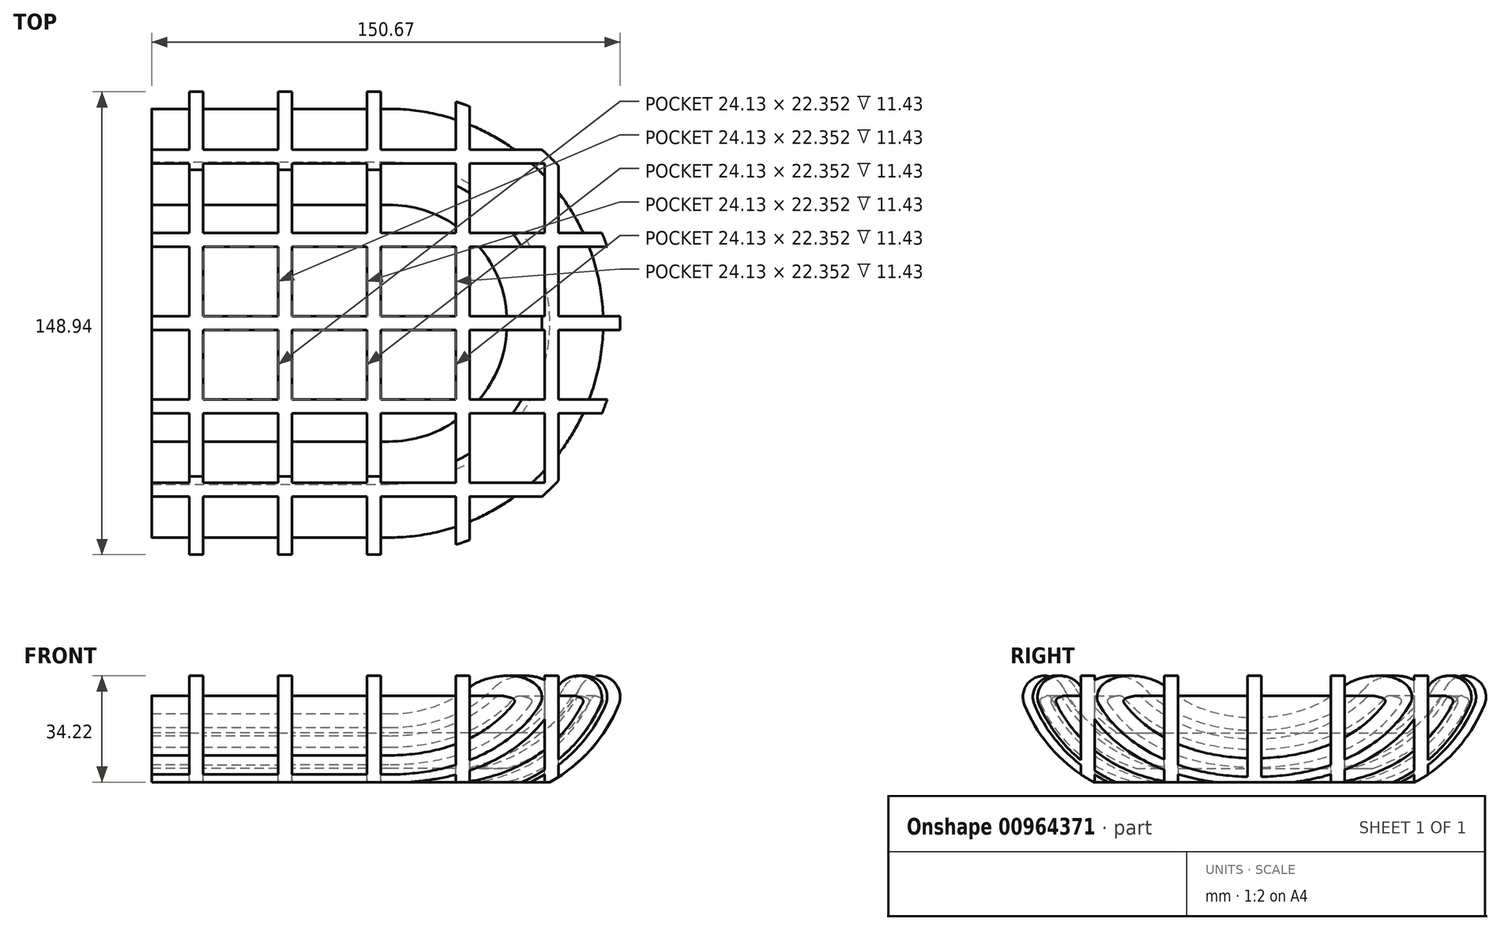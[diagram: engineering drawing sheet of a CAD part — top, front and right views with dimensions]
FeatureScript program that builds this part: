
annotation { "Feature Type Name" : "Feature", "Feature Type Description" : "" }
export const myFeature = defineFeature(function(context is Context, id is Id, definition is map)
    precondition{}
    {
        {
            var Q0;
            Q0=qCreatedBy(makeId("Top.planeOp"),FACE);
            var sketch = newSketch(context, id + "F0", { "sketchPlane" : qUnion([Q0])});
            skArc(sketch, "E0", {"start": v(-76.2, 38.1) * mm, "mid": v(-114.3, 0) * mm, "end": v(-76.2, -38.1) * mm});
            skArc(sketch, "E1", {"start": v(76.2, -38.1) * mm, "mid": v(114.3, 0) * mm, "end": v(76.2, 38.1) * mm});
            skLineSegment(sketch, "E2", {"start": v(-76.2, 38.1) * mm, "end": v(76.2, 38.1) * mm});
            skLineSegment(sketch, "E3", {"start": v(-76.2, -38.1) * mm, "end": v(76.2, -38.1) * mm});
            skLineSegment(sketch, "E4", {"start": v(-76.2, 0) * mm, "end": v(0, 0) * mm, "construction": true});
            skLineSegment(sketch, "E5", {"start": v(76.2, 0) * mm, "end": v(0, 0) * mm, "construction": true});
            skSolve(sketch);
        }
        {
            var Q0;
            Q0=qSketchRegion(id+"F0",true);
            extrude(context, id + "F1", {"entities" : qUnion([Q0]), "depth" : 4.44 * mm, "offsetDistance" : 25.4 * mm});
        }
        {
            var Q0;
            Q0=qCreatedBy(makeId("Right.planeOp"),FACE);
            var Q1;
            Q1=sQuery(id+"F0.wireOp",VERTEX,"E0.end");
            cPlane(context, id + "F2", {"entities" : qUnion([Q0, Q1]), "cplaneType" : CPlaneType.PLANE_POINT, "offset" : 25.4 * mm, "width" : 152.4 * mm, "height" : 152.4 * mm});
        }
        {
            var Q0;
            Q0=qCreatedBy(id+"F2.planeOp",FACE);
            var sketch = newSketch(context, id + "F3", { "sketchPlane" : qUnion([Q0])});
            skArc(sketch, "E6", {"start": v(-69.38, 26.7) * mm, "mid": v(-56.98, 9.56) * mm, "end": v(-38.1, 0) * mm});
            skArc(sketch, "E7", {"start": v(-65.92, 28.11) * mm, "mid": v(-54.33, 13.55) * mm, "end": v(-38.1, 4.44) * mm});
            skLineSegment(sketch, "E8", {"start": v(-65.92, 28.11) * mm, "end": v(-69.38, 26.7) * mm});
            skLineSegment(sketch, "E9", {"start": v(-38.1, 4.45) * mm, "end": v(-38.1, 0) * mm});
            skSolve(sketch);
        }
        {
            var Q0;
            Q0=makeQuery(id+"F3.imprint","IMPRINT",FACE,{"disambiguationData":[TD([[makeQuery(id+"F3.imprint","IMPRINT",EDGE,{"derivedFrom":sQuery(id+"F3.wireOp",EDGE,"E6")}),1.0]])]});
            var Q1;
            Q1=sQuery(id+"F0.wireOp",EDGE,"E0");
            var Q2;
            Q2=sQuery(id+"F0.wireOp",EDGE,"E2");
            var Q3;
            Q3=sQuery(id+"F0.wireOp",EDGE,"E1");
            var Q4;
            Q4=sQuery(id+"F0.wireOp",EDGE,"E3");
            sweep(context, id + "F4", {"profiles" : qUnion([Q0]), "path" : qUnion([Q1, Q2, Q3, Q4])});
        }
        {
            var Q0;
            Q0=qCreatedBy(makeId("Top.planeOp"),FACE);
            cPlane(context, id + "F5", {"entities" : qUnion([Q0]), "cplaneType" : CPlaneType.OFFSET, "offset" : 50.8 * mm, "width" : 152.4 * mm, "height" : 152.4 * mm});
        }
        {
            var Q0;
            Q0=qCreatedBy(id+"F5.planeOp",FACE);
            var sketch = newSketch(context, id + "F6", { "sketchPlane" : qUnion([Q0])});
            skLineSegment(sketch, "E10.bottom", {"start": v(-159.38, 120.18) * mm, "end": v(-154.94, 120.18) * mm});
            skLineSegment(sketch, "E10.top", {"start": v(-159.38, -120.18) * mm, "end": v(-154.94, -120.18) * mm});
            skLineSegment(sketch, "E10.left", {"start": v(-159.38, 120.18) * mm, "end": v(-159.38, -120.18) * mm});
            skLineSegment(sketch, "E10.right", {"start": v(-154.94, 120.18) * mm, "end": v(-154.94, -120.18) * mm});
            skLineSegment(sketch, "E11.bottom", {"start": v(-130.8, 120.18) * mm, "end": v(-126.37, 120.18) * mm});
            skLineSegment(sketch, "E11.top", {"start": v(-130.8, -120.18) * mm, "end": v(-126.36, -120.18) * mm});
            skLineSegment(sketch, "E11.left", {"start": v(-130.8, 120.18) * mm, "end": v(-130.8, -120.18) * mm});
            skLineSegment(sketch, "E11.right", {"start": v(-126.37, 120.18) * mm, "end": v(-126.37, -120.18) * mm});
            skLineSegment(sketch, "E12.bottom", {"start": v(-102.23, 120.18) * mm, "end": v(-97.79, 120.18) * mm});
            skLineSegment(sketch, "E12.top", {"start": v(-102.23, -120.18) * mm, "end": v(-97.79, -120.18) * mm});
            skLineSegment(sketch, "E12.left", {"start": v(-102.23, 120.18) * mm, "end": v(-102.23, -120.18) * mm});
            skLineSegment(sketch, "E12.right", {"start": v(-97.79, 120.18) * mm, "end": v(-97.79, -120.18) * mm});
            skLineSegment(sketch, "E13.bottom", {"start": v(-73.66, 120.18) * mm, "end": v(-69.21, 120.18) * mm});
            skLineSegment(sketch, "E13.top", {"start": v(-73.66, -120.18) * mm, "end": v(-69.21, -120.18) * mm});
            skLineSegment(sketch, "E13.left", {"start": v(-73.66, 120.18) * mm, "end": v(-73.66, -120.18) * mm});
            skLineSegment(sketch, "E13.right", {"start": v(-69.21, 120.18) * mm, "end": v(-69.21, -120.18) * mm});
            skLineSegment(sketch, "E14.bottom", {"start": v(-45.08, 120.18) * mm, "end": v(-40.64, 120.18) * mm});
            skLineSegment(sketch, "E14.top", {"start": v(-45.08, -120.18) * mm, "end": v(-40.64, -120.18) * mm});
            skLineSegment(sketch, "E14.left", {"start": v(-45.08, 120.18) * mm, "end": v(-45.08, -120.18) * mm});
            skLineSegment(sketch, "E14.right", {"start": v(-40.64, 120.18) * mm, "end": v(-40.64, -120.18) * mm});
            skLineSegment(sketch, "E15", {"start": v(-154.94, 120.18) * mm, "end": v(-130.8, 120.18) * mm, "construction": true});
            skLineSegment(sketch, "E16", {"start": v(-126.37, 120.18) * mm, "end": v(-102.23, 120.18) * mm, "construction": true});
            skLineSegment(sketch, "E17", {"start": v(-69.21, 120.18) * mm, "end": v(-45.08, 120.18) * mm, "construction": true});
            skLineSegment(sketch, "E18", {"start": v(-97.79, 120.18) * mm, "end": v(-73.66, 120.18) * mm, "construction": true});
            skLineSegment(sketch, "E19", {"start": v(0, 0) * mm, "end": v(-159.38, 0) * mm, "construction": true});
            skLineSegment(sketch, "E20", {"start": v(-40.64, 120.18) * mm, "end": v(-16.5, 120.18) * mm, "construction": true});
            skLineSegment(sketch, "E21.bottom", {"start": v(-16.5, 120.18) * mm, "end": v(-12.06, 120.18) * mm});
            skLineSegment(sketch, "E21.top", {"start": v(-16.5, -120.18) * mm, "end": v(-12.06, -120.18) * mm});
            skLineSegment(sketch, "E21.left", {"start": v(-16.5, 120.18) * mm, "end": v(-16.51, -120.18) * mm});
            skLineSegment(sketch, "E21.right", {"start": v(-12.06, 120.18) * mm, "end": v(-12.07, -120.18) * mm});
            skLineSegment(sketch, "E22.bottom", {"start": v(12.07, 120.18) * mm, "end": v(16.51, 120.18) * mm});
            skLineSegment(sketch, "E22.top", {"start": v(12.07, -120.18) * mm, "end": v(16.51, -120.18) * mm});
            skLineSegment(sketch, "E22.left", {"start": v(12.07, 120.18) * mm, "end": v(12.07, -120.18) * mm});
            skLineSegment(sketch, "E22.right", {"start": v(16.51, 120.18) * mm, "end": v(16.51, -120.18) * mm});
            skLineSegment(sketch, "E23.bottom", {"start": v(40.64, 120.18) * mm, "end": v(45.09, 120.18) * mm});
            skLineSegment(sketch, "E23.top", {"start": v(40.64, -120.18) * mm, "end": v(45.09, -120.18) * mm});
            skLineSegment(sketch, "E23.left", {"start": v(40.64, 120.18) * mm, "end": v(40.64, -120.18) * mm});
            skLineSegment(sketch, "E23.right", {"start": v(45.09, 120.18) * mm, "end": v(45.09, -120.18) * mm});
            skLineSegment(sketch, "E24.bottom", {"start": v(69.22, 120.18) * mm, "end": v(73.66, 120.18) * mm});
            skLineSegment(sketch, "E24.top", {"start": v(69.22, -120.18) * mm, "end": v(73.66, -120.18) * mm});
            skLineSegment(sketch, "E24.left", {"start": v(69.22, 120.18) * mm, "end": v(69.22, -120.18) * mm});
            skLineSegment(sketch, "E24.right", {"start": v(73.66, 120.18) * mm, "end": v(73.66, -120.18) * mm});
            skLineSegment(sketch, "E25.bottom", {"start": v(97.8, 120.18) * mm, "end": v(102.24, 120.18) * mm});
            skLineSegment(sketch, "E25.top", {"start": v(97.8, -120.18) * mm, "end": v(102.24, -120.18) * mm});
            skLineSegment(sketch, "E25.left", {"start": v(97.8, 120.18) * mm, "end": v(97.8, -120.18) * mm});
            skLineSegment(sketch, "E25.right", {"start": v(102.24, 120.18) * mm, "end": v(102.24, -120.18) * mm});
            skLineSegment(sketch, "E26.bottom", {"start": v(126.37, 120.18) * mm, "end": v(130.81, 120.18) * mm});
            skLineSegment(sketch, "E26.top", {"start": v(126.37, -120.18) * mm, "end": v(130.81, -120.18) * mm});
            skLineSegment(sketch, "E26.left", {"start": v(126.37, 120.18) * mm, "end": v(126.37, -120.18) * mm});
            skLineSegment(sketch, "E26.right", {"start": v(130.81, 120.18) * mm, "end": v(130.81, -120.18) * mm});
            skLineSegment(sketch, "E27", {"start": v(102.24, 120.18) * mm, "end": v(126.37, 120.18) * mm, "construction": true});
            skLineSegment(sketch, "E28", {"start": v(73.66, 120.18) * mm, "end": v(97.8, 120.18) * mm, "construction": true});
            skLineSegment(sketch, "E29", {"start": v(45.09, 120.18) * mm, "end": v(69.22, 120.18) * mm, "construction": true});
            skLineSegment(sketch, "E30", {"start": v(16.51, 120.18) * mm, "end": v(40.64, 120.18) * mm, "construction": true});
            skLineSegment(sketch, "E31", {"start": v(-12.06, 120.18) * mm, "end": v(12.07, 120.18) * mm, "construction": true});
            skLineSegment(sketch, "E32", {"start": v(-12.06, 0) * mm, "end": v(0, 69.38) * mm, "construction": true});
            skLineSegment(sketch, "E33", {"start": v(0, 69.38) * mm, "end": v(12.07, 0) * mm, "construction": true});
            skLineSegment(sketch, "E34.bottom", {"start": v(154.94, 120.18) * mm, "end": v(159.39, 120.18) * mm});
            skLineSegment(sketch, "E34.top", {"start": v(154.94, -120.18) * mm, "end": v(159.39, -120.18) * mm});
            skLineSegment(sketch, "E34.left", {"start": v(154.94, 120.18) * mm, "end": v(154.94, -120.18) * mm});
            skLineSegment(sketch, "E34.right", {"start": v(159.39, 120.18) * mm, "end": v(159.39, -120.18) * mm});
            skLineSegment(sketch, "E35", {"start": v(130.81, 120.18) * mm, "end": v(154.94, 120.18) * mm});
            skSolve(sketch);
        }
        {
            var Q0;
            Q0=qSketchRegion(id+"F6",true);
            extrude(context, id + "F7", {"entities" : qUnion([Q0]), "oppositeDirection" : true, "depth" : 63.5 * mm, "offsetDistance" : 25.4 * mm});
        }
        {
            var Q0;
            Q0=qCreatedBy(id+"F5.planeOp",FACE);
            var sketch = newSketch(context, id + "F8", { "sketchPlane" : qUnion([Q0])});
            skLineSegment(sketch, "E36.bottom", {"start": v(-183.68, 2.22) * mm, "end": v(183.68, 2.22) * mm});
            skLineSegment(sketch, "E36.top", {"start": v(-183.68, -2.22) * mm, "end": v(183.68, -2.22) * mm});
            skLineSegment(sketch, "E36.left", {"start": v(-183.68, 2.22) * mm, "end": v(-183.68, -2.22) * mm});
            skLineSegment(sketch, "E36.right", {"start": v(183.68, 2.22) * mm, "end": v(183.68, -2.22) * mm});
            skLineSegment(sketch, "E37.bottom", {"start": v(-183.68, 29.02) * mm, "end": v(183.68, 29.02) * mm});
            skLineSegment(sketch, "E37.top", {"start": v(-183.68, 24.57) * mm, "end": v(183.68, 24.57) * mm});
            skLineSegment(sketch, "E37.left", {"start": v(-183.68, 29.02) * mm, "end": v(-183.68, 24.57) * mm});
            skLineSegment(sketch, "E37.right", {"start": v(183.68, 29.02) * mm, "end": v(183.68, 24.57) * mm});
            skLineSegment(sketch, "E38.bottom", {"start": v(-183.68, 55.82) * mm, "end": v(183.68, 55.82) * mm});
            skLineSegment(sketch, "E38.top", {"start": v(-183.68, 51.37) * mm, "end": v(183.68, 51.37) * mm});
            skLineSegment(sketch, "E38.left", {"start": v(-183.68, 55.82) * mm, "end": v(-183.68, 51.37) * mm});
            skLineSegment(sketch, "E38.right", {"start": v(183.68, 55.82) * mm, "end": v(183.68, 51.37) * mm});
            skLineSegment(sketch, "E39.bottom", {"start": v(-183.68, -24.57) * mm, "end": v(183.68, -24.57) * mm});
            skLineSegment(sketch, "E39.top", {"start": v(-183.68, -29.02) * mm, "end": v(183.68, -29.02) * mm});
            skLineSegment(sketch, "E39.left", {"start": v(-183.68, -24.57) * mm, "end": v(-183.68, -29.02) * mm});
            skLineSegment(sketch, "E39.right", {"start": v(183.68, -24.57) * mm, "end": v(183.68, -29.02) * mm});
            skLineSegment(sketch, "E40.bottom", {"start": v(-183.68, -51.37) * mm, "end": v(183.68, -51.37) * mm});
            skLineSegment(sketch, "E40.top", {"start": v(-183.68, -55.82) * mm, "end": v(183.68, -55.82) * mm});
            skLineSegment(sketch, "E40.left", {"start": v(-183.68, -51.37) * mm, "end": v(-183.68, -55.82) * mm});
            skLineSegment(sketch, "E40.right", {"start": v(183.68, -51.37) * mm, "end": v(183.68, -55.82) * mm});
            skLineSegment(sketch, "E41", {"start": v(183.68, 51.37) * mm, "end": v(183.68, 29.02) * mm, "construction": true});
            skLineSegment(sketch, "E42", {"start": v(183.68, 24.57) * mm, "end": v(183.68, 2.22) * mm, "construction": true});
            skLineSegment(sketch, "E43", {"start": v(183.68, -2.22) * mm, "end": v(183.68, -24.57) * mm, "construction": true});
            skLineSegment(sketch, "E44", {"start": v(183.68, -29.02) * mm, "end": v(183.68, -51.37) * mm, "construction": true});
            skLineSegment(sketch, "E45", {"start": v(0, 0) * mm, "end": v(0, 2.22) * mm, "construction": true});
            skLineSegment(sketch, "E46", {"start": v(0, 0) * mm, "end": v(183.68, 0) * mm, "construction": true});
            skLineSegment(sketch, "E47", {"start": v(0, 0) * mm, "end": v(0, -2.22) * mm, "construction": true});
            skSolve(sketch);
        }
        {
            var Q0;
            Q0=qSketchRegion(id+"F8",true);
            extrude(context, id + "F9", {"entities" : qUnion([Q0]), "oppositeDirection" : true, "depth" : 63.5 * mm, "offsetDistance" : 25.4 * mm});
        }
        {
            var Q0;
            Q0=makeQuery(id+"F4.opSweep","SWEPT_EDGE",EDGE,{"disambiguationData":[OSD([sQuery(id+"F0.wireOp",EDGE,"E0"),sQuery(id+"F3.wireOp",EDGE,"E6"),sQuery(id+"F3.wireOp",EDGE,"E8")])]});
            fillet(context, id + "F10", {"entities" : qUnion([Q0]), "radius" : 1.27 * mm, "tangentPropagation" : true, "allowEdgeOverflow" : false});
        }
        {
            var Q0;
            Q0=makeQuery(id+"F4.opSweep","SWEPT_EDGE",EDGE,{"disambiguationData":[OSD([sQuery(id+"F0.wireOp",EDGE,"E0"),sQuery(id+"F3.wireOp",EDGE,"E7"),sQuery(id+"F3.wireOp",EDGE,"E8")])]});
            fillet(context, id + "F11", {"entities" : qUnion([Q0]), "radius" : 1.27 * mm, "tangentPropagation" : true, "allowEdgeOverflow" : false});
        }
        {
            var Q0;
            Q0=makeQuery(id+"F4.opSweep","SWEPT_BODY",BODY,{"disambiguationData":[OSD([sQuery(id+"F0.wireOp",EDGE,"E2"),sQuery(id+"F3.wireOp",EDGE,"E6"),sQuery(id+"F3.wireOp",EDGE,"E7"),sQuery(id+"F3.wireOp",EDGE,"E8"),sQuery(id+"F3.wireOp",EDGE,"E9")])]});
            var Q1;
            Q1=makeQuery(id+"F7.opExtrude","SWEPT_BODY",BODY,{"disambiguationData":[OSD([sQuery(id+"F6.wireOp",EDGE,"E10.bottom"),sQuery(id+"F6.wireOp",EDGE,"E10.top"),sQuery(id+"F6.wireOp",EDGE,"E10.left"),sQuery(id+"F6.wireOp",EDGE,"E10.right")])]});
            var Q2;
            Q2=makeQuery(id+"F7.opExtrude","SWEPT_BODY",BODY,{"disambiguationData":[OSD([sQuery(id+"F6.wireOp",EDGE,"E11.bottom"),sQuery(id+"F6.wireOp",EDGE,"E11.top"),sQuery(id+"F6.wireOp",EDGE,"E11.left"),sQuery(id+"F6.wireOp",EDGE,"E11.right")])]});
            var Q3;
            Q3=makeQuery(id+"F7.opExtrude","SWEPT_BODY",BODY,{"disambiguationData":[OSD([sQuery(id+"F6.wireOp",EDGE,"E12.bottom"),sQuery(id+"F6.wireOp",EDGE,"E12.top"),sQuery(id+"F6.wireOp",EDGE,"E12.left"),sQuery(id+"F6.wireOp",EDGE,"E12.right")])]});
            var Q4;
            Q4=makeQuery(id+"F7.opExtrude","SWEPT_BODY",BODY,{"disambiguationData":[OSD([sQuery(id+"F6.wireOp",EDGE,"E13.bottom"),sQuery(id+"F6.wireOp",EDGE,"E13.top"),sQuery(id+"F6.wireOp",EDGE,"E13.left"),sQuery(id+"F6.wireOp",EDGE,"E13.right")])]});
            var Q5;
            Q5=makeQuery(id+"F7.opExtrude","SWEPT_BODY",BODY,{"disambiguationData":[OSD([sQuery(id+"F6.wireOp",EDGE,"E14.bottom"),sQuery(id+"F6.wireOp",EDGE,"E14.top"),sQuery(id+"F6.wireOp",EDGE,"E14.left"),sQuery(id+"F6.wireOp",EDGE,"E14.right")])]});
            var Q6;
            Q6=makeQuery(id+"F7.opExtrude","SWEPT_BODY",BODY,{"disambiguationData":[OSD([sQuery(id+"F6.wireOp",EDGE,"E21.bottom"),sQuery(id+"F6.wireOp",EDGE,"E21.top"),sQuery(id+"F6.wireOp",EDGE,"E21.left"),sQuery(id+"F6.wireOp",EDGE,"E21.right")])]});
            var Q7;
            Q7=makeQuery(id+"F7.opExtrude","SWEPT_BODY",BODY,{"disambiguationData":[OSD([sQuery(id+"F6.wireOp",EDGE,"E22.bottom"),sQuery(id+"F6.wireOp",EDGE,"E22.top"),sQuery(id+"F6.wireOp",EDGE,"E22.left"),sQuery(id+"F6.wireOp",EDGE,"E22.right")])]});
            var Q8;
            Q8=makeQuery(id+"F7.opExtrude","SWEPT_BODY",BODY,{"disambiguationData":[OSD([sQuery(id+"F6.wireOp",EDGE,"E23.bottom"),sQuery(id+"F6.wireOp",EDGE,"E23.top"),sQuery(id+"F6.wireOp",EDGE,"E23.left"),sQuery(id+"F6.wireOp",EDGE,"E23.right")])]});
            var Q9;
            Q9=makeQuery(id+"F7.opExtrude","SWEPT_BODY",BODY,{"disambiguationData":[OSD([sQuery(id+"F6.wireOp",EDGE,"E24.bottom"),sQuery(id+"F6.wireOp",EDGE,"E24.top"),sQuery(id+"F6.wireOp",EDGE,"E24.left"),sQuery(id+"F6.wireOp",EDGE,"E24.right")])]});
            var Q10;
            Q10=makeQuery(id+"F7.opExtrude","SWEPT_BODY",BODY,{"disambiguationData":[OSD([sQuery(id+"F6.wireOp",EDGE,"E25.bottom"),sQuery(id+"F6.wireOp",EDGE,"E25.top"),sQuery(id+"F6.wireOp",EDGE,"E25.left"),sQuery(id+"F6.wireOp",EDGE,"E25.right")])]});
            var Q11;
            Q11=makeQuery(id+"F7.opExtrude","SWEPT_BODY",BODY,{"disambiguationData":[OSD([sQuery(id+"F6.wireOp",EDGE,"E26.bottom"),sQuery(id+"F6.wireOp",EDGE,"E26.top"),sQuery(id+"F6.wireOp",EDGE,"E26.left"),sQuery(id+"F6.wireOp",EDGE,"E26.right")])]});
            var Q12;
            Q12=makeQuery(id+"F7.opExtrude","SWEPT_BODY",BODY,{"disambiguationData":[OSD([sQuery(id+"F6.wireOp",EDGE,"E34.bottom"),sQuery(id+"F6.wireOp",EDGE,"E34.top"),sQuery(id+"F6.wireOp",EDGE,"E34.left"),sQuery(id+"F6.wireOp",EDGE,"E34.right")])]});
            var Q13;
            Q13=makeQuery(id+"F9.opExtrude","SWEPT_BODY",BODY,{"disambiguationData":[OSD([sQuery(id+"F8.wireOp",EDGE,"E36.bottom"),sQuery(id+"F8.wireOp",EDGE,"E36.top"),sQuery(id+"F8.wireOp",EDGE,"E36.left"),sQuery(id+"F8.wireOp",EDGE,"E36.right")])]});
            var Q14;
            Q14=makeQuery(id+"F9.opExtrude","SWEPT_BODY",BODY,{"disambiguationData":[OSD([sQuery(id+"F8.wireOp",EDGE,"E37.bottom"),sQuery(id+"F8.wireOp",EDGE,"E37.top"),sQuery(id+"F8.wireOp",EDGE,"E37.left"),sQuery(id+"F8.wireOp",EDGE,"E37.right")])]});
            var Q15;
            Q15=makeQuery(id+"F9.opExtrude","SWEPT_BODY",BODY,{"disambiguationData":[OSD([sQuery(id+"F8.wireOp",EDGE,"E38.bottom"),sQuery(id+"F8.wireOp",EDGE,"E38.top"),sQuery(id+"F8.wireOp",EDGE,"E38.left"),sQuery(id+"F8.wireOp",EDGE,"E38.right")])]});
            var Q16;
            Q16=makeQuery(id+"F9.opExtrude","SWEPT_BODY",BODY,{"disambiguationData":[OSD([sQuery(id+"F8.wireOp",EDGE,"E39.bottom"),sQuery(id+"F8.wireOp",EDGE,"E39.top"),sQuery(id+"F8.wireOp",EDGE,"E39.left"),sQuery(id+"F8.wireOp",EDGE,"E39.right")])]});
            var Q17;
            Q17=makeQuery(id+"F9.opExtrude","SWEPT_BODY",BODY,{"disambiguationData":[OSD([sQuery(id+"F8.wireOp",EDGE,"E40.bottom"),sQuery(id+"F8.wireOp",EDGE,"E40.top"),sQuery(id+"F8.wireOp",EDGE,"E40.left"),sQuery(id+"F8.wireOp",EDGE,"E40.right")])]});
            var Q18;
            Q18=makeQuery(id+"F1.opExtrude","SWEPT_BODY",BODY,{"disambiguationData":[OSD([sQuery(id+"F0.wireOp",EDGE,"E0"),sQuery(id+"F0.wireOp",EDGE,"E1"),sQuery(id+"F0.wireOp",EDGE,"E2"),sQuery(id+"F0.wireOp",EDGE,"E3")])]});
            booleanBodies(context, id + "F12", {"operationType" : BooleanOperationType.UNION, "tools" : qUnion([Q0, Q1, Q2, Q3, Q4, Q5, Q6, Q7, Q8, Q9, Q10, Q11, Q12, Q13, Q14, Q15, Q16, Q17, Q18])});
        }
        {
            var Q0;
            Q0=qCreatedBy(id+"F2.planeOp",FACE);
            var sketch = newSketch(context, id + "F13", { "sketchPlane" : qUnion([Q0])});
            skArc(sketch, "E48", {"start": v(-61.6, 30.53) * mm, "mid": v(-70.5, 33.6) * mm, "end": v(-73.96, 24.82) * mm});
            skArc(sketch, "E49", {"start": v(-73.96, 24.82) * mm, "mid": v(-64.07, 9.48) * mm, "end": v(-49.31, -1.27) * mm});
            skLineSegment(sketch, "E50", {"start": v(-49.31, -1.27) * mm, "end": v(0, -1.27) * mm});
            skLineSegment(sketch, "E51", {"start": v(0, -1.27) * mm, "end": v(0, 0) * mm});
            skLineSegment(sketch, "E52", {"start": v(0, 0) * mm, "end": v(0, 15.88) * mm});
            skLineSegment(sketch, "E53", {"start": v(0, 15.88) * mm, "end": v(-49.31, 15.87) * mm});
            skArc(sketch, "E54", {"start": v(-61.6, 30.53) * mm, "mid": v(-56.27, 22.52) * mm, "end": v(-49.31, 15.88) * mm});
            skLineSegment(sketch, "E55", {"start": v(0, 15.88) * mm, "end": v(0, 76.2) * mm});
            skLineSegment(sketch, "E56", {"start": v(0, -1.27) * mm, "end": v(0, -38.1) * mm});
            skLineSegment(sketch, "E57", {"start": v(0, -38.1) * mm, "end": v(-158.28, -38.1) * mm});
            skLineSegment(sketch, "E58", {"start": v(-158.28, -38.1) * mm, "end": v(-158.28, 76.2) * mm});
            skLineSegment(sketch, "E59", {"start": v(-158.28, 76.2) * mm, "end": v(0, 76.2) * mm});
            skSolve(sketch);
        }
        {
            var Q0;
            Q0=qCreatedBy(id+"F2.planeOp",FACE);
            var sketch = newSketch(context, id + "F14", { "sketchPlane" : qUnion([Q0])});
            skArc(sketch, "E60.0", {"start": v(-61.6, 30.53) * mm, "mid": v(-56.27, 22.52) * mm, "end": v(-49.31, 15.88) * mm});
            skArc(sketch, "E60.1", {"start": v(-73.96, 24.82) * mm, "mid": v(-64.07, 9.48) * mm, "end": v(-49.31, -1.27) * mm});
            skArc(sketch, "E61.0", {"start": v(-61.6, 30.53) * mm, "mid": v(-70.5, 33.6) * mm, "end": v(-73.96, 24.82) * mm});
            skLineSegment(sketch, "E62", {"start": v(-49.31, 15.88) * mm, "end": v(-49.31, 76.2) * mm});
            skLineSegment(sketch, "E63", {"start": v(-49.31, 76.2) * mm, "end": v(-158.28, 76.2) * mm});
            skLineSegment(sketch, "E64", {"start": v(-158.28, 76.2) * mm, "end": v(-158.28, -38.1) * mm});
            skLineSegment(sketch, "E65", {"start": v(-158.28, -38.1) * mm, "end": v(-49.31, -38.1) * mm});
            skLineSegment(sketch, "E66", {"start": v(-49.31, -38.1) * mm, "end": v(-49.31, -1.27) * mm});
            skSolve(sketch);
        }
        {
            var Q0;
            Q0=makeQuery(id+"F14.imprint","IMPRINT",FACE,{"disambiguationData":[TD([[makeQuery(id+"F14.imprint","IMPRINT",EDGE,{"derivedFrom":sQuery(id+"F14.wireOp",EDGE,"E60.0")}),1.0]])]});
            var Q1;
            Q1=sQuery(id+"F0.wireOp",EDGE,"E0");
            var Q2;
            Q2=sQuery(id+"F0.wireOp",EDGE,"E2");
            var Q3;
            Q3=sQuery(id+"F0.wireOp",EDGE,"E1");
            var Q4;
            Q4=sQuery(id+"F0.wireOp",EDGE,"E3");
            sweep(context, id + "F15", {"operationType" : NewBodyOperationType.REMOVE, "profiles" : qUnion([Q0]), "path" : qUnion([Q1, Q2, Q3, Q4])});
        }
        {
            var Q0;
            Q0=qCreatedBy(makeId("Top.planeOp"),FACE);
            var Q1;
            Q1=sQuery(id+"F13.wireOp",VERTEX,"E53.end");
            cPlane(context, id + "F16", {"entities" : qUnion([Q0, Q1]), "cplaneType" : CPlaneType.PLANE_POINT, "offset" : 25.4 * mm, "width" : 152.4 * mm, "height" : 152.4 * mm});
        }
        {
            var Q0;
            Q0=qCreatedBy(makeId("Top.planeOp"),FACE);
            var Q1;
            Q1=sQuery(id+"F13.wireOp",VERTEX,"E49.end");
            cPlane(context, id + "F17", {"entities" : qUnion([Q0, Q1]), "cplaneType" : CPlaneType.PLANE_POINT, "offset" : 25.4 * mm, "width" : 152.4 * mm, "height" : 152.4 * mm});
        }
        {
            var Q0;
            Q0=qCreatedBy(id+"F16.planeOp",FACE);
            var sketch = newSketch(context, id + "F18", { "sketchPlane" : qUnion([Q0])});
            skArc(sketch, "E67", {"start": v(-76.2, 49.31) * mm, "mid": v(-125.51, 0) * mm, "end": v(-76.2, -49.31) * mm});
            skArc(sketch, "E68", {"start": v(76.2, -49.31) * mm, "mid": v(125.51, 0) * mm, "end": v(76.2, 49.31) * mm});
            skLineSegment(sketch, "E69", {"start": v(-76.2, 49.31) * mm, "end": v(76.2, 49.31) * mm});
            skLineSegment(sketch, "E70", {"start": v(-76.2, -49.31) * mm, "end": v(76.2, -49.31) * mm});
            skLineSegment(sketch, "E71", {"start": v(-76.2, 0) * mm, "end": v(0, 0) * mm, "construction": true});
            skLineSegment(sketch, "E72", {"start": v(0, 0) * mm, "end": v(76.2, 0) * mm, "construction": true});
            skSolve(sketch);
        }
        {
            var Q0;
            Q0=qCreatedBy(id+"F17.planeOp",FACE);
            var sketch = newSketch(context, id + "F19", { "sketchPlane" : qUnion([Q0])});
            skArc(sketch, "E73", {"start": v(-76.2, 49.31) * mm, "mid": v(-125.51, 0) * mm, "end": v(-76.2, -49.31) * mm});
            skArc(sketch, "E74", {"start": v(76.2, -49.31) * mm, "mid": v(125.51, 0) * mm, "end": v(76.2, 49.31) * mm});
            skLineSegment(sketch, "E75", {"start": v(-76.2, 49.31) * mm, "end": v(76.2, 49.31) * mm});
            skLineSegment(sketch, "E76", {"start": v(76.2, -49.31) * mm, "end": v(-76.2, -49.31) * mm});
            skLineSegment(sketch, "E77", {"start": v(-76.2, 0) * mm, "end": v(0, 0) * mm, "construction": true});
            skLineSegment(sketch, "E78", {"start": v(0, 0) * mm, "end": v(76.2, 0) * mm, "construction": true});
            skSolve(sketch);
        }
        {
            var Q0;
            Q0=qSketchRegion(id+"F18",true);
            extrude(context, id + "F20", {"entities" : qUnion([Q0]), "operationType" : NewBodyOperationType.REMOVE, "endBound" : BoundingType.THROUGH_ALL, "depth" : 25.4 * mm, "offsetDistance" : 25.4 * mm});
        }
        {
            var Q0;
            Q0=qSketchRegion(id+"F19",true);
            extrude(context, id + "F21", {"entities" : qUnion([Q0]), "operationType" : NewBodyOperationType.REMOVE, "endBound" : BoundingType.THROUGH_ALL, "oppositeDirection" : true, "depth" : 25.4 * mm, "offsetDistance" : 25.4 * mm});
        }
        {
            var Q0;
            Q0=makeQuery(id+"F12.opBoolean","SPLIT",FACE,{"disambiguationData":[TD([makeQuery(id+"F7.opExtrude","SWEPT_FACE",FACE,{"disambiguationData":[OSD([sQuery(id+"F6.wireOp",EDGE,"E21.right")])]}),makeQuery(id+"F7.opExtrude","SWEPT_FACE",FACE,{"disambiguationData":[OSD([sQuery(id+"F6.wireOp",EDGE,"E22.left")])]}),makeQuery(id+"F9.opExtrude","SWEPT_FACE",FACE,{"disambiguationData":[OSD([sQuery(id+"F8.wireOp",EDGE,"E36.top")])]}),makeQuery(id+"F9.opExtrude","SWEPT_FACE",FACE,{"disambiguationData":[OSD([sQuery(id+"F8.wireOp",EDGE,"E39.bottom")])]})])],"derivedFrom":makeQuery(id+"F1.opExtrude","CAP_FACE",FACE,{"disambiguationData":[OSD([sQuery(id+"F0.wireOp",EDGE,"E0"),sQuery(id+"F0.wireOp",EDGE,"E1"),sQuery(id+"F0.wireOp",EDGE,"E2"),sQuery(id+"F0.wireOp",EDGE,"E3")])],"isStart":true})});
            var sketch = newSketch(context, id + "F22", { "sketchPlane" : qUnion([Q0])});
            skLineSegment(sketch, "E79.bottom", {"start": v(-186.73, 109.48) * mm, "end": v(188.77, 109.48) * mm});
            skLineSegment(sketch, "E79.top", {"start": v(-186.73, -123.25) * mm, "end": v(188.77, -123.25) * mm});
            skLineSegment(sketch, "E79.left", {"start": v(-186.73, 109.48) * mm, "end": v(-186.73, -123.25) * mm});
            skLineSegment(sketch, "E79.right", {"start": v(188.77, 109.48) * mm, "end": v(188.77, -123.25) * mm});
            skSolve(sketch);
        }
        {
            var Q0;
            Q0=qSketchRegion(id+"F22",true);
            extrude(context, id + "F23", {"entities" : qUnion([Q0]), "operationType" : NewBodyOperationType.REMOVE, "endBound" : BoundingType.THROUGH_ALL, "depth" : 25.4 * mm, "offsetDistance" : 25.4 * mm});
        }
        {
            var Q0;
            Q0=qCreatedBy(makeId("Right.planeOp"),FACE);
            var sketch = newSketch(context, id + "F24", { "sketchPlane" : qUnion([Q0])});
            skLineSegment(sketch, "E80.bottom", {"start": v(-118.91, 61.26) * mm, "end": v(129.71, 61.26) * mm});
            skLineSegment(sketch, "E80.top", {"start": v(-118.91, -61.26) * mm, "end": v(129.71, -61.26) * mm});
            skLineSegment(sketch, "E80.left", {"start": v(-118.91, 61.26) * mm, "end": v(-118.91, -61.26) * mm});
            skLineSegment(sketch, "E80.right", {"start": v(129.71, 61.26) * mm, "end": v(129.71, -61.26) * mm});
            skLineSegment(sketch, "E81", {"start": v(0, 0) * mm, "end": v(129.71, 0) * mm, "construction": true});
            skLineSegment(sketch, "E82", {"start": v(0, 61.26) * mm, "end": v(0, 0) * mm, "construction": true});
            skSolve(sketch);
        }
        {
            var Q0;
            Q0 = qSketchRegion(id + "F24", true);
            extrude(context, id + "F25", {"entities" : qUnion([Q0]), "operationType" : NewBodyOperationType.REMOVE, "endBound" : BoundingType.THROUGH_ALL, "oppositeDirection" : true, "depth" : 25.4 * mm, "offsetDistance" : 25.4 * mm});
        }
    });
